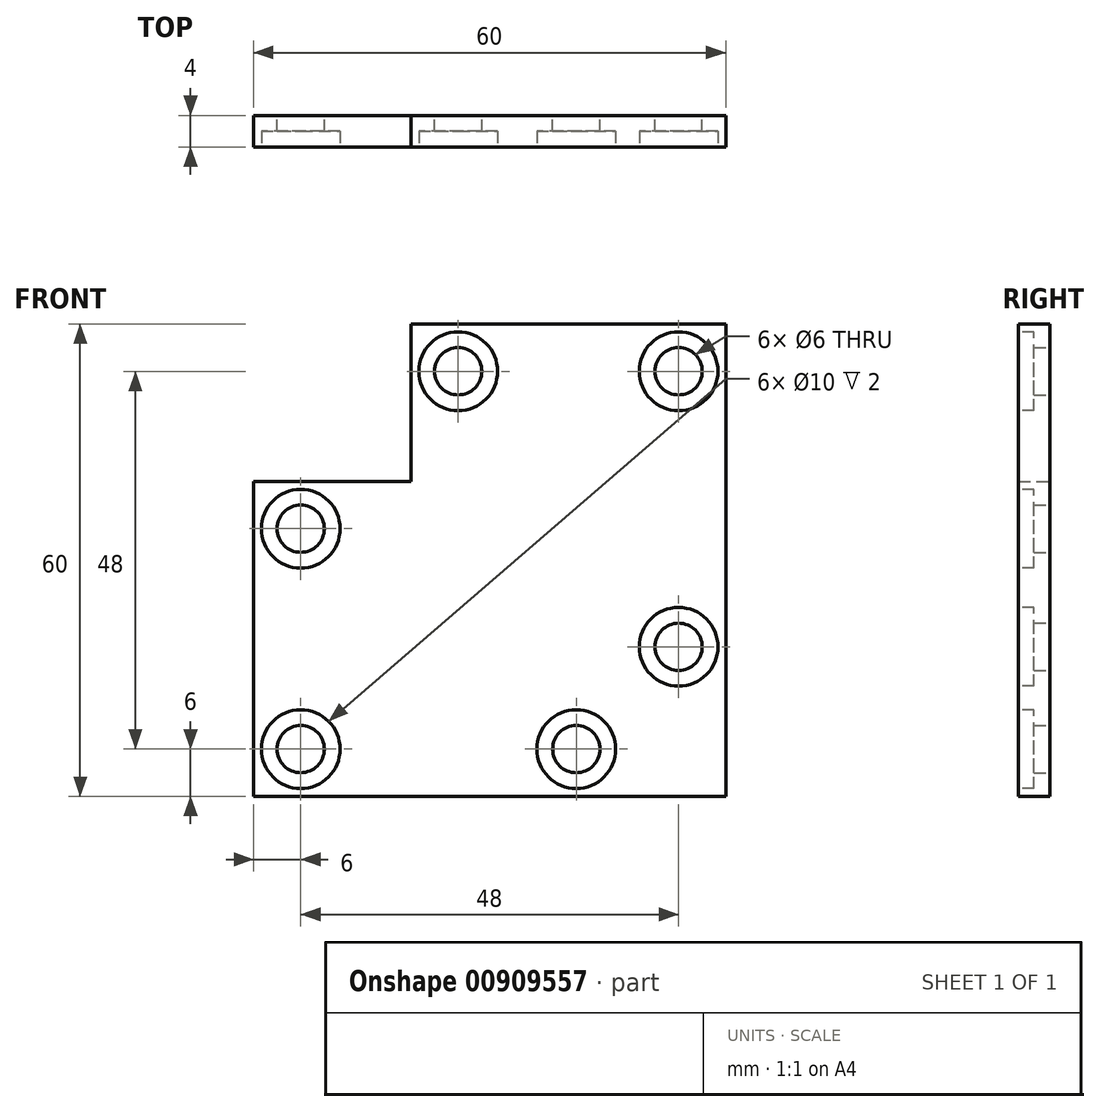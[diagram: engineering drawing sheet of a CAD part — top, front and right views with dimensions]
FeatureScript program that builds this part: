
annotation { "Feature Type Name" : "Feature", "Feature Type Description" : "" }
export const myFeature = defineFeature(function(context is Context, id is Id, definition is map)
    precondition{}
    {
        {
            var Q0;
            Q0=qCreatedBy(makeId("Front.planeOp"),FACE);
            var sketch = newSketch(context, id + "F0", { "sketchPlane" : qUnion([Q0])});
            skLineSegment(sketch, "E0.bottom", {"start": v(0, 0) * mm, "end": v(-60, 0) * mm});
            skLineSegment(sketch, "E0.top", {"start": v(-40, 40) * mm, "end": v(-60, 40) * mm});
            skLineSegment(sketch, "E0.left", {"start": v(0, 0) * mm, "end": v(0, 40) * mm});
            skLineSegment(sketch, "E0.right", {"start": v(-60, 0) * mm, "end": v(-60, 40) * mm});
            skLineSegment(sketch, "E1.top", {"start": v(0, 60) * mm, "end": v(-40, 60) * mm});
            skLineSegment(sketch, "E1.left", {"start": v(0, 40) * mm, "end": v(0, 60) * mm});
            skLineSegment(sketch, "E1.right", {"start": v(-40, 40) * mm, "end": v(-40, 60) * mm});
            skLineSegment(sketch, "E2", {"start": v(0, 0) * mm, "end": v(-40, 40) * mm, "construction": true});
            skCircle(sketch, "E3", {"center": v(-54, 34) * mm, "radius": 3 * mm});
            skCircle(sketch, "E4", {"center": v(-54, 6) * mm, "radius": 3 * mm});
            skCircle(sketch, "E5", {"center": v(-19, 6) * mm, "radius": 3 * mm});
            skCircle(sketch, "E6", {"center": v(-34, 54) * mm, "radius": 3 * mm});
            skCircle(sketch, "E7", {"center": v(-6, 54) * mm, "radius": 3 * mm});
            skCircle(sketch, "E8", {"center": v(-6, 19) * mm, "radius": 3 * mm});
            skSolve(sketch);
        }
        {
            var Q0;
            Q0=makeQuery(id+"F0.imprint","IMPRINT",FACE,{"disambiguationData":[TD([[makeQuery(id+"F0.imprint","IMPRINT",EDGE,{"derivedFrom":sQuery(id+"F0.wireOp",EDGE,"E0.bottom")}),-1.0]])]});
            extrude(context, id + "F1", {"entities" : qUnion([Q0]), "depth" : 4 * mm, "offsetDistance" : 25 * mm});
        }
        {
            var Q0;
            Q0=makeQuery(id+"F1.opExtrude","CAP_FACE",FACE,{"disambiguationData":[OSD([sQuery(id+"F0.wireOp",EDGE,"E0.bottom"),sQuery(id+"F0.wireOp",EDGE,"E0.top"),sQuery(id+"F0.wireOp",EDGE,"E0.left"),sQuery(id+"F0.wireOp",EDGE,"E0.right"),sQuery(id+"F0.wireOp",EDGE,"E1.top"),sQuery(id+"F0.wireOp",EDGE,"E1.left"),sQuery(id+"F0.wireOp",EDGE,"E1.right"),sQuery(id+"F0.wireOp",EDGE,"E3"),sQuery(id+"F0.wireOp",EDGE,"E4"),sQuery(id+"F0.wireOp",EDGE,"E5"),sQuery(id+"F0.wireOp",EDGE,"E6"),sQuery(id+"F0.wireOp",EDGE,"E7"),sQuery(id+"F0.wireOp",EDGE,"E8")])],"isStart":false});
            var sketch = newSketch(context, id + "F2", { "sketchPlane" : qUnion([Q0])});
            skCircle(sketch, "E9", {"center": v(-54, 34) * mm, "radius": 5 * mm});
            skCircle(sketch, "E10", {"center": v(-54, 6) * mm, "radius": 5 * mm});
            skCircle(sketch, "E11", {"center": v(-19, 6) * mm, "radius": 5 * mm});
            skCircle(sketch, "E12", {"center": v(-6, 19) * mm, "radius": 5 * mm});
            skCircle(sketch, "E13", {"center": v(-34, 54) * mm, "radius": 5 * mm});
            skCircle(sketch, "E14", {"center": v(-6, 54) * mm, "radius": 5 * mm});
            skSolve(sketch);
        }
        {
            var Q0;
            Q0=makeQuery(id+"F2.imprint","IMPRINT",FACE,{"disambiguationData":[TD([[makeQuery(id+"F2.imprint","IMPRINT",EDGE,{"derivedFrom":sQuery(id+"F2.wireOp",EDGE,"E9")}),1.0]])]});
            var Q1;
            Q1=makeQuery(id+"F2.imprint","IMPRINT",FACE,{"disambiguationData":[TD([[makeQuery(id+"F2.imprint","IMPRINT",EDGE,{"derivedFrom":sQuery(id+"F2.wireOp",EDGE,"E13")}),1.0]])]});
            var Q2;
            Q2=makeQuery(id+"F2.imprint","IMPRINT",FACE,{"disambiguationData":[TD([[makeQuery(id+"F2.imprint","IMPRINT",EDGE,{"derivedFrom":sQuery(id+"F2.wireOp",EDGE,"E14")}),1.0]])]});
            var Q3;
            Q3=makeQuery(id+"F2.imprint","IMPRINT",FACE,{"disambiguationData":[TD([[makeQuery(id+"F2.imprint","IMPRINT",EDGE,{"derivedFrom":sQuery(id+"F2.wireOp",EDGE,"E12")}),1.0]])]});
            var Q4;
            Q4=makeQuery(id+"F2.imprint","IMPRINT",FACE,{"disambiguationData":[TD([[makeQuery(id+"F2.imprint","IMPRINT",EDGE,{"derivedFrom":sQuery(id+"F2.wireOp",EDGE,"E11")}),1.0]])]});
            var Q5;
            Q5=makeQuery(id+"F2.imprint","IMPRINT",FACE,{"disambiguationData":[TD([[makeQuery(id+"F2.imprint","IMPRINT",EDGE,{"derivedFrom":sQuery(id+"F2.wireOp",EDGE,"E10")}),1.0]])]});
            extrude(context, id + "F3", {"entities" : qUnion([Q0, Q1, Q2, Q3, Q4, Q5]), "operationType" : NewBodyOperationType.REMOVE, "oppositeDirection" : true, "depth" : 2 * mm, "offsetDistance" : 25 * mm});
        }
    });
